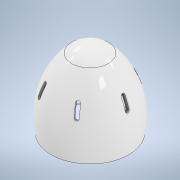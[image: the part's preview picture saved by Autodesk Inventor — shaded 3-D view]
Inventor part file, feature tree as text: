
AUTODESK INVENTOR PART (.ipt)
format: ipt  version: 2020 (Build 240168000, 168)  size: 477,696 bytes
history: native  units: in
note: dims shown in document units (in); Inventor stores cm internally (conversion verified against a paired STEP export)
features: other x5, revolve x4, helix x2, boolean_combine x2, thread x2, extrude x1, pattern_circular x1, shell x1, sketch x1
ambient origin geometry x8: Origin, YZ Plane, XZ Plane, XY Plane, X Axis, Y Axis, Z Axis, Center Point
bodies: Solid1 (feature_tree), Solid2 (feature_tree), Solid3 (feature_tree)
feature tree (19):
  other  "SmartEgg Shell.ipt"
  revolve  "Revolution1"  Angle=90.0deg
  helix  "Coil1"  [1 undecoded]
  helix  "Coil2"  [1 undecoded]
  revolve  "Revolution2"  Angle=90.0deg
  other  "Extra Cutout"
  revolve  "Revolution3"  [1 undecoded]
  boolean_combine  "Combine1"
  extrude  "Extrusion1"  Depth=0.3937in
  pattern_circular  "Circular Pattern1"  [2 undecoded]
  boolean_combine  "Combine2"
  revolve  "Revolution4"  Angle=360.0deg
  shell  "Shell Sketch"  Thickness=90.0deg
  thread  "Thread Sketch"  [1 undecoded]
  thread  "Thread Mask"  [1 undecoded]
  other  "Top Thread Mask"
  other  "Vent Plane"
  sketch  "Sketch6"  dims[d0=0.3937in d1=90.0deg d2=0.3706in d3=1.0in d4=1.1811in d5=0.0in d6=90.0deg d7=90.0deg d8=0.0in d9=0.0in d10=0.3706in d11=1.0in d12=1.1811in d13=0.0in d14=90.0deg d15=90.0deg d16=0.0in d17=0.0in d18=90.0deg d19=0.0984in d20=0.2953in d21=0.3937in d22=0.0in d23=2.3622in d24=360.0deg d30=90.0deg d31=0.0098in d32=0.1969in d33=90.0deg]
  other  "Vent Lookup"
note: 7 required parameter values undecoded (feature->parameter linkage not recoverable at this tier; creation-order binding heuristic only, values carry confidence <= 0.55)